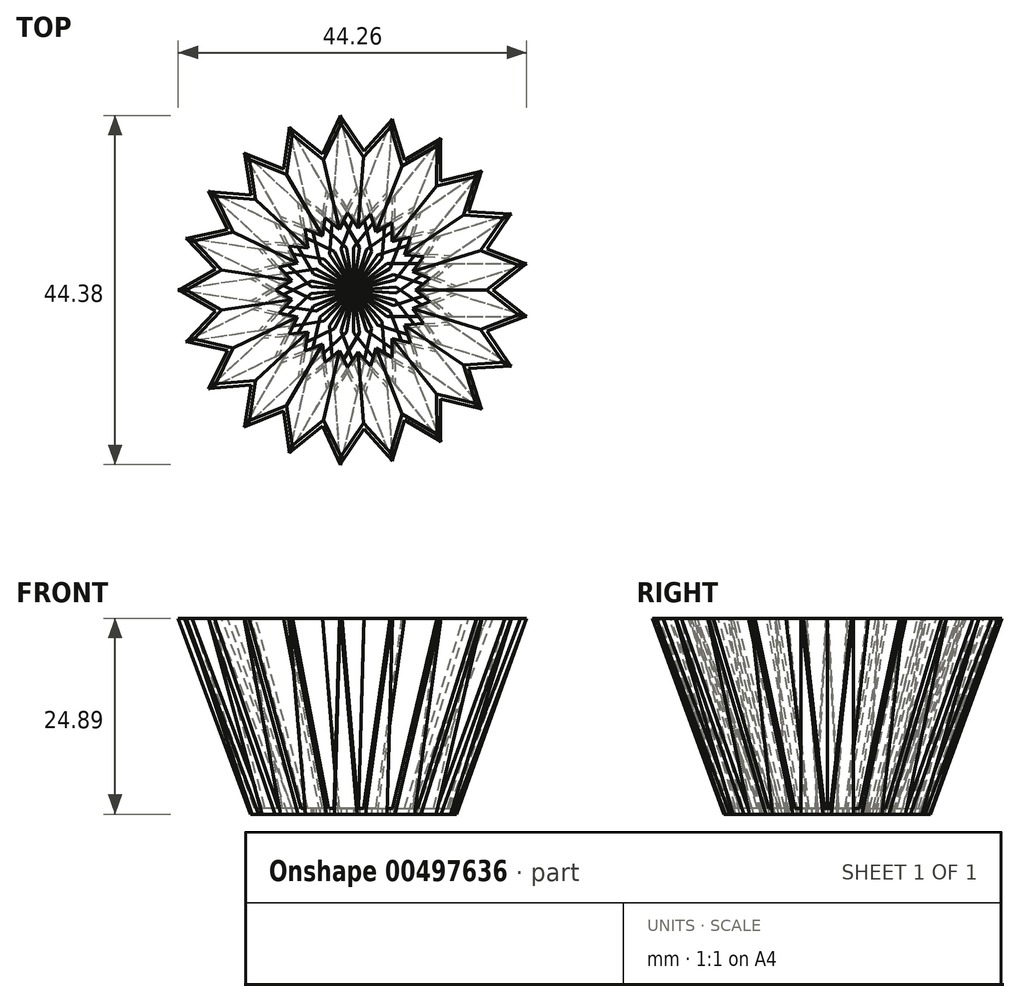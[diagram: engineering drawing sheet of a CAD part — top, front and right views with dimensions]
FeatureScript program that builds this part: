
annotation { "Feature Type Name" : "Feature", "Feature Type Description" : "" }
export const myFeature = defineFeature(function(context is Context, id is Id, definition is map)
    precondition{}
    {
        {
            var Q0;
            Q0=qCreatedBy(makeId("Front.planeOp"),FACE);
            var sketch = newSketch(context, id + "F0", { "sketchPlane" : qUnion([Q0])});
            skLineSegment(sketch, "E0", {"start": v(0, 0) * mm, "end": v(8.4, 0) * mm});
            skLineSegment(sketch, "E1", {"start": v(8.4, 0) * mm, "end": v(17.73, 24.89) * mm});
            skLineSegment(sketch, "E2", {"start": v(17.73, 24.89) * mm, "end": v(14.25, 52.02) * mm});
            skLineSegment(sketch, "E3.0", {"start": v(15.58, 25.14) * mm, "end": v(12.13, 52.02) * mm});
            skLineSegment(sketch, "E3.1", {"start": v(6.95, 2.1) * mm, "end": v(15.58, 25.14) * mm});
            skLineSegment(sketch, "E3.2", {"start": v(0, 2.1) * mm, "end": v(6.95, 2.1) * mm});
            skLineSegment(sketch, "E4", {"start": v(14.25, 52.02) * mm, "end": v(12.13, 52.02) * mm});
            skLineSegment(sketch, "E5", {"start": v(0, 2.1) * mm, "end": v(0, 0) * mm});
            skLineSegment(sketch, "E6", {"start": v(17.73, 24.89) * mm, "end": v(15.49, 24.89) * mm});
            skLineSegment(sketch, "E7.0", {"start": v(7.89, 0.75) * mm, "end": v(17.03, 25.15) * mm});
            skLineSegment(sketch, "E7.1", {"start": v(0, 0.75) * mm, "end": v(7.89, 0.75) * mm});
            skSolve(sketch);
        }
        {
            var Q0;
            Q0=qCreatedBy(makeId("Top.planeOp"),FACE);
            var sketch = newSketch(context, id + "F1", { "sketchPlane" : qUnion([Q0])});
            skLineSegment(sketch, "E8", {"start": v(0, 0) * mm, "end": v(0.83, 1.39) * mm});
            skLineSegment(sketch, "E9", {"start": v(0.83, 1.39) * mm, "end": v(1.36, 4.85) * mm});
            skPoint(sketch, "E10.orphan", {"position": v(1.65, 2.78) * mm});
            skPoint(sketch, "E11.orphan", {"position": v(1.65, 6.74) * mm});
            skLineSegment(sketch, "E12", {"start": v(0, 0) * mm, "end": v(4.27, 3.35) * mm});
            skSolve(sketch);
        }
        {
            var Q0;
            {var subQ1=sQuery(id+"F0.wireOp",EDGE,"E0");Q0=makeQuery(id+"F0.imprint","IMPRINT",FACE,{"disambiguationData":[TD([[makeQuery(id+"F0.imprint","IMPRINT",EDGE,{"derivedFrom":subQ1}),1.0]])]});}
            var Q1;
            Q1=sQuery(id+"F1.wireOp",EDGE,"E12");
            sweep(context, id + "F2", {"profiles" : qUnion([Q0]), "path" : qUnion([Q1])});
        }
        {
            var Q0;
            Q0=makeQuery(id+"F2.opSweep","SWEPT_BODY",BODY,{"disambiguationData":[OSD([sQuery(id+"F0.wireOp",EDGE,"E0"),sQuery(id+"F0.wireOp",EDGE,"E1"),sQuery(id+"F0.wireOp",EDGE,"E5"),sQuery(id+"F0.wireOp",EDGE,"E6"),sQuery(id+"F0.wireOp",EDGE,"E7.0"),sQuery(id+"F0.wireOp",EDGE,"E7.1"),sQuery(id+"F1.wireOp",EDGE,"E8")])]});
            var Q1;
            {var subQ1=sQuery(id+"F0.wireOp",EDGE,"E3.2");Q1=makeQuery(id+"F0.imprint","IMPRINT",FACE,{"disambiguationData":[TD([[makeQuery(id+"F0.imprint","IMPRINT",EDGE,{"derivedFrom":subQ1}),-1.0]])]});}
            mirror(context, id + "F3", {"operationType" : NewBodyOperationType.ADD, "entities" : qUnion([Q0]), "mirrorPlane" : qUnion([Q1])});
        }
        {
            var Q0;
            Q0=makeQuery(id+"F2.opSweep","SWEPT_BODY",BODY,{"disambiguationData":[OSD([sQuery(id+"F0.wireOp",EDGE,"E0"),sQuery(id+"F0.wireOp",EDGE,"E1"),sQuery(id+"F0.wireOp",EDGE,"E5"),sQuery(id+"F0.wireOp",EDGE,"E6"),sQuery(id+"F0.wireOp",EDGE,"E7.0"),sQuery(id+"F0.wireOp",EDGE,"E7.1"),sQuery(id+"F1.wireOp",EDGE,"E8")])]});
            var Q1;
            Q1=sQuery(id+"F0.wireOp",EDGE,"E5");
            circularPattern(context, id + "F4", {"entities" : qUnion([Q0]), "axis" : qUnion([Q1]), "angle" : 360 * degree, "instanceCount" : 21, "equalSpace" : true});
        }
    });
